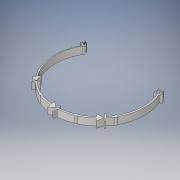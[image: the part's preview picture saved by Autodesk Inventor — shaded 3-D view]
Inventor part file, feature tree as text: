
AUTODESK INVENTOR PART (.ipt)
format: ipt  version: 2016 (Build 200138000, 138)  size: 425,984 bytes
history: native  units: in
note: dims shown in document units (in); Inventor stores cm internally (conversion verified against a paired STEP export)
features: sketch x2, revolve x1, extrude x1, projected_geometry x1
ambient origin geometry x8: Origin, YZ Plane, XZ Plane, XY Plane, X Axis, Y Axis, Z Axis, Center Point
bodies: Solid1 (feature_tree)
feature tree (5):
  revolve  "Revolution1"  [1 undecoded]
  extrude  "Extrusion1"  Depth=0.1in
  sketch  "Sketch1"  dims[d0=0.8265in d1=0.175in]
  sketch  "Sketch2"  dims[d2=0.05in d3=0.1in d4=0.15in d5=0.275in d6=90.0deg d7=0.1in d18=0.05in d21=0.025in d22=0.125in d23=0.8in d24=0.025in d25=0.0125in d26=0.05in d27=0.025in d28=0.0125in d29=0.135in d30=0.135in d31=0.025in d32=0.025in d33=0.0125in d34=0.15in d35=0.05in d36=0.3in d37=0.025in d38=0.0125in d39=0.135in d40=0.3in d42=0.025in d43=0.135in d44=0.0451in d45=0.0451in d46=0.025in d47=0.0125in d48=0.05in d49=0.3in d50=0.025in d51=0.0125in d52=0.3in d53=0.135in d54=0.025in d55=0.135in d56=0.05in d57=0.025in d58=0.0125in d59=0.15in d60=0.135in d61=0.1in d62=0.075in d63=0.025in d64=0.025in d65=0.025in d66=0.8in d67=0.025in d68=0.0125in d69=0.1in d70=0.0in]
  projected_geometry  "Projected Loop1"
note: 1 required parameter value undecoded (feature->parameter linkage not recoverable at this tier; creation-order binding heuristic only, values carry confidence <= 0.55)
